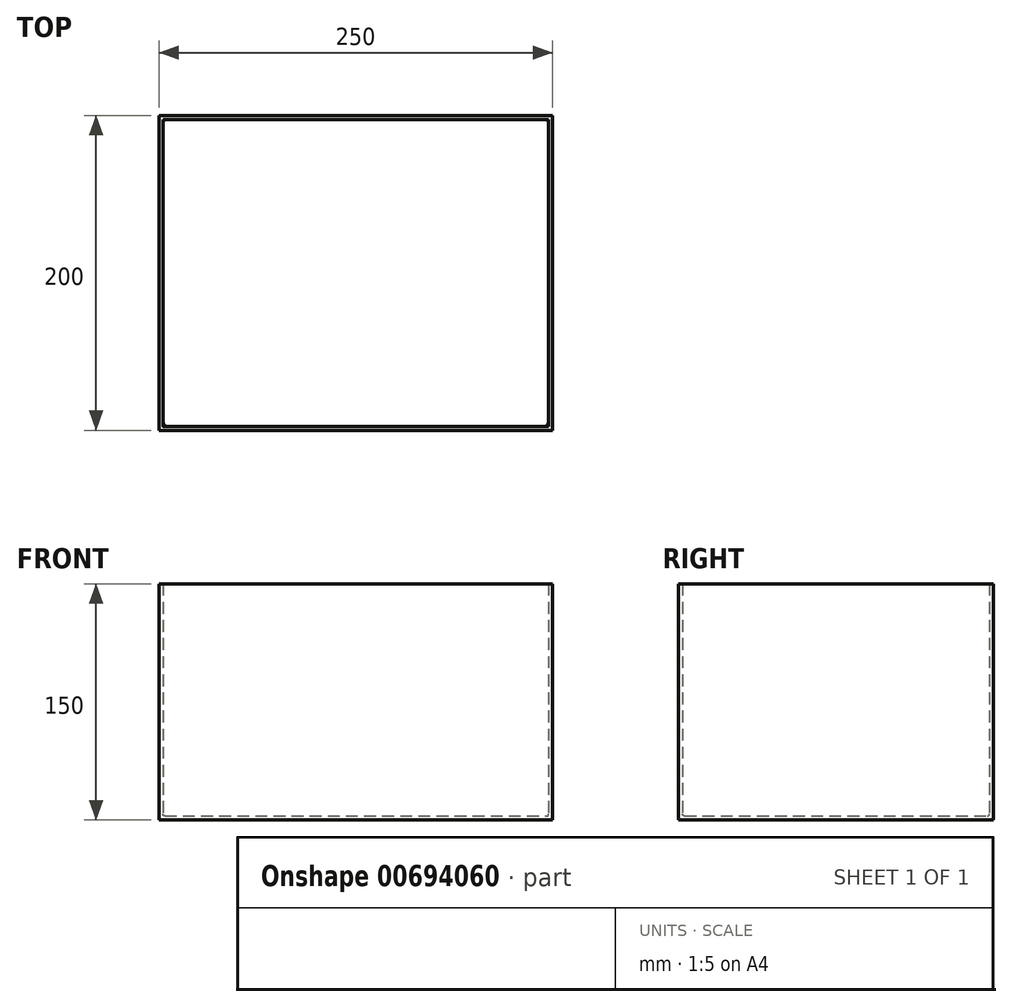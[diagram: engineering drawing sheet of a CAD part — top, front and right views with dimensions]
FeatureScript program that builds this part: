
annotation { "Feature Type Name" : "Feature", "Feature Type Description" : "" }
export const myFeature = defineFeature(function(context is Context, id is Id, definition is map)
    precondition{}
    {
        {
            var Q0;
            Q0=qCreatedBy(makeId("Top.planeOp"),FACE);
            var sketch = newSketch(context, id + "F0", { "sketchPlane" : qUnion([Q0])});
            skLineSegment(sketch, "E0.bottom", {"start": v(0, 0) * mm, "end": v(250, 0) * mm});
            skLineSegment(sketch, "E0.top", {"start": v(0, 200) * mm, "end": v(250, 200) * mm});
            skLineSegment(sketch, "E0.left", {"start": v(0, 0) * mm, "end": v(0, 200) * mm});
            skLineSegment(sketch, "E0.right", {"start": v(250, 0) * mm, "end": v(250, 200) * mm});
            skSolve(sketch);
        }
        {
            var Q0;
            Q0=makeQuery(id+"F0.imprint","IMPRINT",FACE,{"disambiguationData":[TD([[makeQuery(id+"F0.imprint","IMPRINT",EDGE,{"derivedFrom":sQuery(id+"F0.wireOp",EDGE,"E0.bottom")}),1.0]])]});
            extrude(context, id + "F1", {"entities" : qUnion([Q0]), "depth" : 150 * mm, "offsetDistance" : 25 * mm});
        }
        {
            var Q0;
            Q0=makeQuery(id+"F1.opExtrude","CAP_FACE",FACE,{"disambiguationData":[OSD([sQuery(id+"F0.wireOp",EDGE,"E0.bottom"),sQuery(id+"F0.wireOp",EDGE,"E0.top"),sQuery(id+"F0.wireOp",EDGE,"E0.left"),sQuery(id+"F0.wireOp",EDGE,"E0.right")])],"isStart":false});
            shell(context, id + "F2", {"entities" : qUnion([Q0]), "thickness" : 2.5 * mm});
        }
        {
            var Q0;
            {var subQ0=sQuery(id+"F0.wireOp",EDGE,"E0.left");Q0=makeQuery(id+"F2.opShell","OFFSET_EDGE",EDGE,{"disambiguationData":[OSD([subQ0]),TDD([makeQuery(id+"F1.opExtrude","CAP_EDGE",EDGE,{"disambiguationData":[OSD([subQ0])],"isStart":true})])]});}
            var Q1;
            {var subQ0=sQuery(id+"F0.wireOp",EDGE,"E0.top");Q1=makeQuery(id+"F2.opShell","OFFSET_EDGE",EDGE,{"disambiguationData":[OSD([subQ0]),TDD([makeQuery(id+"F1.opExtrude","CAP_EDGE",EDGE,{"disambiguationData":[OSD([subQ0])],"isStart":true})])]});}
            var Q2;
            {var subQ0=sQuery(id+"F0.wireOp",EDGE,"E0.right");Q2=makeQuery(id+"F2.opShell","OFFSET_EDGE",EDGE,{"disambiguationData":[OSD([subQ0]),TDD([makeQuery(id+"F1.opExtrude","CAP_EDGE",EDGE,{"disambiguationData":[OSD([subQ0])],"isStart":true})])]});}
            var Q3;
            {var subQ0=sQuery(id+"F0.wireOp",EDGE,"E0.bottom");Q3=makeQuery(id+"F2.opShell","OFFSET_EDGE",EDGE,{"disambiguationData":[OSD([subQ0]),TDD([makeQuery(id+"F1.opExtrude","CAP_EDGE",EDGE,{"disambiguationData":[OSD([subQ0])],"isStart":true})])]});}
            fillet(context, id + "F3", {"entities" : qUnion([Q0, Q1, Q2, Q3]), "radius" : 1.29 * mm, "tangentPropagation" : true, "allowEdgeOverflow" : false});
        }
    });
